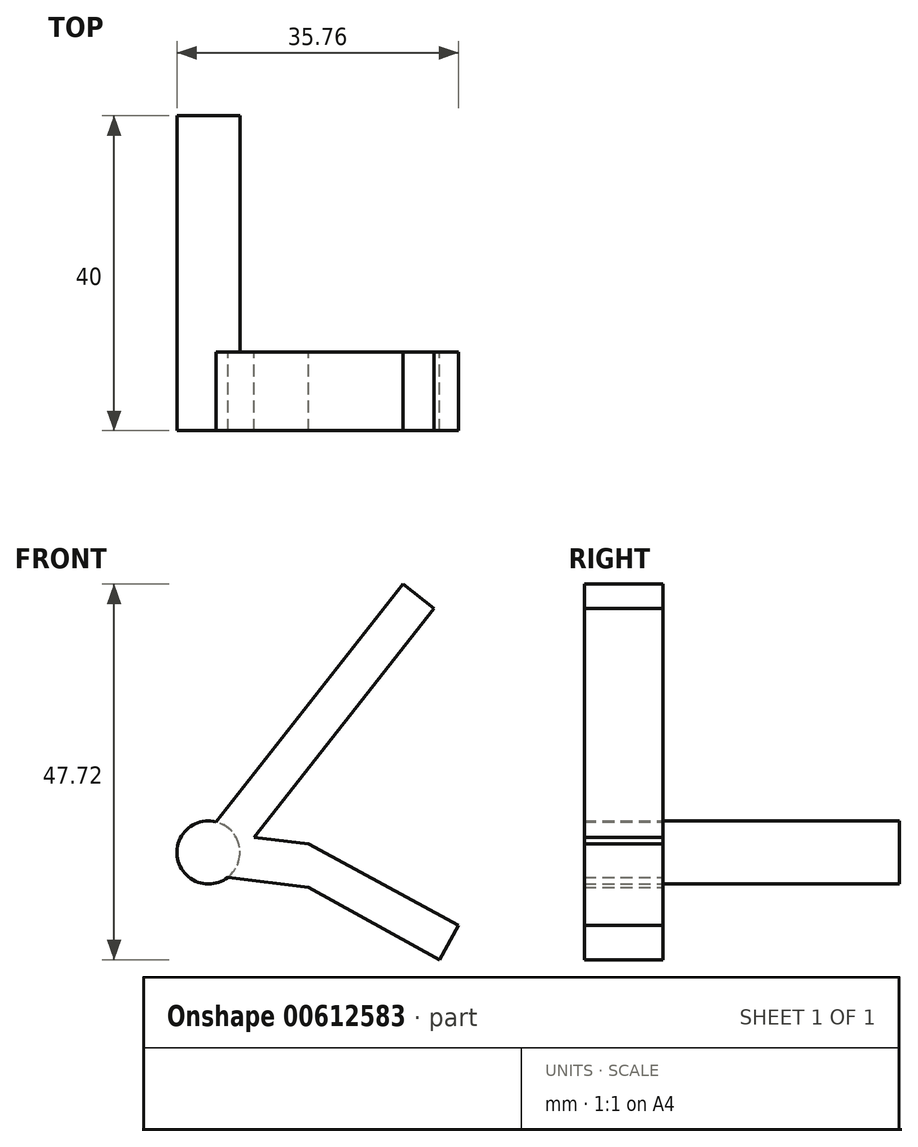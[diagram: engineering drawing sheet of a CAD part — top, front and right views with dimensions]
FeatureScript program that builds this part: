
annotation { "Feature Type Name" : "Feature", "Feature Type Description" : "" }
export const myFeature = defineFeature(function(context is Context, id is Id, definition is map)
    precondition{}
    {
        {
            var Q0;
            Q0=qCreatedBy(makeId("Front.planeOp"),FACE);
            var sketch = newSketch(context, id + "F0", { "sketchPlane" : qUnion([Q0])});
            skCircle(sketch, "E0", {"center": v(0, 0) * mm, "radius": 40 * mm, "construction": true});
            skLineSegment(sketch, "E1", {"start": v(0, 0) * mm, "end": v(0, 62.67) * mm, "construction": true});
            skLineSegment(sketch, "E2", {"start": v(0, 40) * mm, "end": v(16.62, 30.8) * mm});
            skLineSegment(sketch, "E3", {"start": v(16.62, 30.8) * mm, "end": v(19.05, 35.17) * mm});
            skLineSegment(sketch, "E4", {"start": v(19.05, 35.17) * mm, "end": v(0, 45.49) * mm});
            skCircle(sketch, "E5", {"center": v(-12.7, 44.43) * mm, "radius": 4 * mm});
            skLineSegment(sketch, "E6", {"start": v(0, 45.49) * mm, "end": v(-12.7, 47.08) * mm});
            skLineSegment(sketch, "E7", {"start": v(0, 40) * mm, "end": v(-12.7, 41.6) * mm});
            skLineSegment(sketch, "E8", {"start": v(-12.7, 47.08) * mm, "end": v(-12.7, 41.6) * mm});
            skLineSegment(sketch, "E9", {"start": v(-12.7, 47.08) * mm, "end": v(12.03, 78.52) * mm});
            skLineSegment(sketch, "E10", {"start": v(12.03, 78.52) * mm, "end": v(15.96, 75.43) * mm});
            skLineSegment(sketch, "E11", {"start": v(15.96, 75.43) * mm, "end": v(-6.92, 46.36) * mm});
            skSolve(sketch);
        }
        {
            var Q0;
            {var subQ5=sQuery(id+"F0.wireOp",EDGE,"E8");Q0=makeQuery(id+"F0.imprint","IMPRINT",FACE,{"disambiguationData":[TD([[makeQuery(id+"F0.imprint","IMPRINT",EDGE,{"derivedFrom":subQ5}),1.0]])]});}
            var Q1;
            {var subQ5=sQuery(id+"F0.wireOp",EDGE,"E8");Q1=makeQuery(id+"F0.imprint","IMPRINT",FACE,{"disambiguationData":[TD([[makeQuery(id+"F0.imprint","IMPRINT",EDGE,{"derivedFrom":subQ5}),-1.0]])]});}
            var Q2;
            {var subQ0=sQuery(id+"F0.wireOp",EDGE,"E9");var subQ1=sQuery(id+"F0.wireOp",EDGE,"E5");var subQ2=makeQuery(id+"F0.imprint","INTERSECT",VERTEX,{"derivedFrom":[subQ1,subQ0]});Q2=makeQuery(id+"F0.imprint","IMPRINT",FACE,{"disambiguationData":[TD([[makeQuery(id+"F0.imprint","IMPRINT",EDGE,{"disambiguationData":[TD([[subQ2,1.0]])],"derivedFrom":subQ1}),1.0]])]});}
            extrude(context, id + "F1", {"entities" : qUnion([Q0, Q1, Q2]), "depth" : 10 * mm, "offsetDistance" : 25.4 * mm});
        }
        {
            var Q0;
            {var subQ6=sQuery(id+"F0.wireOp",EDGE,"E2");Q0=makeQuery(id+"F0.imprint","IMPRINT",FACE,{"disambiguationData":[TD([[makeQuery(id+"F0.imprint","IMPRINT",EDGE,{"derivedFrom":subQ6}),1.0]])]});}
            var Q1;
            {var subQ0=sQuery(id+"F0.wireOp",EDGE,"E10");Q1=makeQuery(id+"F0.imprint","IMPRINT",FACE,{"disambiguationData":[TD([[makeQuery(id+"F0.imprint","IMPRINT",EDGE,{"derivedFrom":subQ0}),-1.0]])]});}
            extrude(context, id + "F2", {"entities" : qUnion([Q0, Q1]), "operationType" : NewBodyOperationType.ADD, "depth" : 10 * mm, "offsetDistance" : 25.4 * mm});
        }
        {
            var Q0;
            {var subQ5=sQuery(id+"F0.wireOp",EDGE,"E8");Q0=makeQuery(id+"F0.imprint","IMPRINT",FACE,{"disambiguationData":[TD([[makeQuery(id+"F0.imprint","IMPRINT",EDGE,{"derivedFrom":subQ5}),1.0]])]});}
            var Q1;
            {var subQ0=sQuery(id+"F0.wireOp",EDGE,"E9");var subQ1=sQuery(id+"F0.wireOp",EDGE,"E5");var subQ2=makeQuery(id+"F0.imprint","INTERSECT",VERTEX,{"derivedFrom":[subQ1,subQ0]});Q1=makeQuery(id+"F0.imprint","IMPRINT",FACE,{"disambiguationData":[TD([[makeQuery(id+"F0.imprint","IMPRINT",EDGE,{"disambiguationData":[TD([[subQ2,1.0]])],"derivedFrom":subQ1}),1.0]])]});}
            var Q2;
            {var subQ5=sQuery(id+"F0.wireOp",EDGE,"E8");Q2=makeQuery(id+"F0.imprint","IMPRINT",FACE,{"disambiguationData":[TD([[makeQuery(id+"F0.imprint","IMPRINT",EDGE,{"derivedFrom":subQ5}),-1.0]])]});}
            extrude(context, id + "F3", {"entities" : qUnion([Q0, Q1, Q2]), "operationType" : NewBodyOperationType.ADD, "oppositeDirection" : true, "depth" : 30 * mm, "offsetDistance" : 25.4 * mm});
        }
    });
